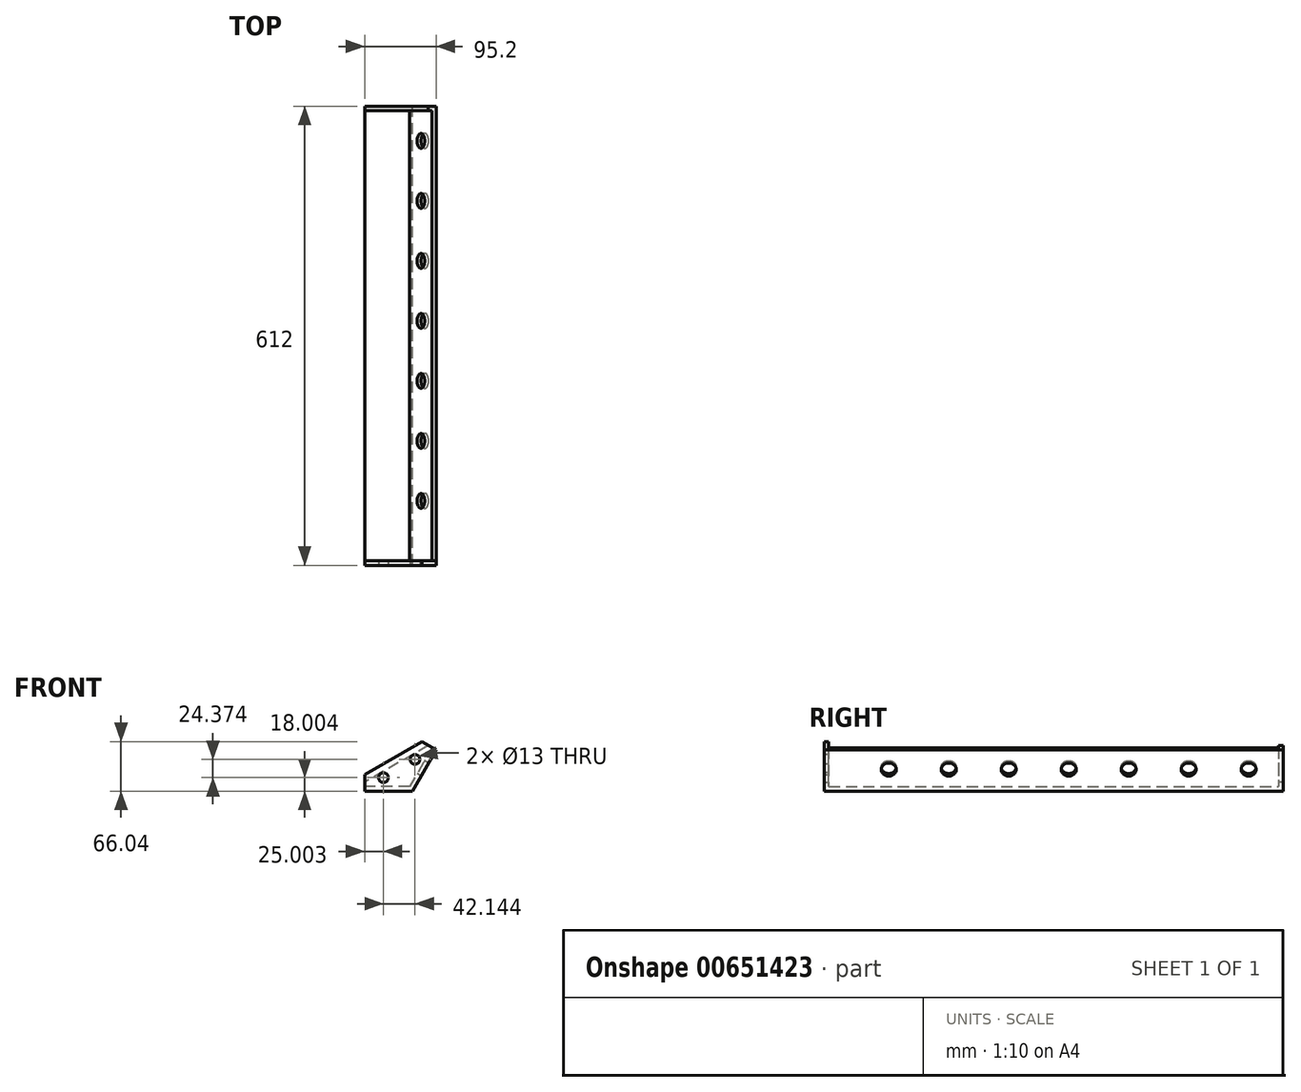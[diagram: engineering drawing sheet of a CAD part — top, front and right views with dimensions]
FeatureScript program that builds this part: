
annotation { "Feature Type Name" : "Feature", "Feature Type Description" : "" }
export const myFeature = defineFeature(function(context is Context, id is Id, definition is map)
    precondition{}
    {
        {
            var Q0;
            Q0=qCreatedBy(makeId("Front.planeOp"),FACE);
            var sketch = newSketch(context, id + "F0", { "sketchPlane" : qUnion([Q0])});
            skLineSegment(sketch, "E0", {"start": v(3.16, -10.39) * mm, "end": v(66.63, -10.39) * mm});
            skLineSegment(sketch, "E1", {"start": v(66.63, -10.39) * mm, "end": v(98.36, 44.58) * mm});
            skLineSegment(sketch, "E2", {"start": v(98.36, 44.58) * mm, "end": v(93.16, 47.58) * mm});
            skLineSegment(sketch, "E3", {"start": v(93.16, 47.58) * mm, "end": v(63.16, -4.39) * mm});
            skLineSegment(sketch, "E4", {"start": v(63.16, -4.39) * mm, "end": v(3.16, -4.39) * mm});
            skLineSegment(sketch, "E5", {"start": v(3.16, -4.39) * mm, "end": v(3.16, -10.39) * mm});
            skSolve(sketch);
        }
        {
            var Q0;
            Q0 = qSketchRegion(id + "F0", true);
            extrude(context, id + "F1", {"entities" : qUnion([Q0]), "depth" : 600 * mm, "offsetDistance" : 25 * mm});
        }
        {
            var Q0;
            Q0=makeQuery(id+"F1.opExtrude","CAP_FACE",FACE,{"disambiguationData":[OSD([sQuery(id+"F0.wireOp",EDGE,"E0"),sQuery(id+"F0.wireOp",EDGE,"E1"),sQuery(id+"F0.wireOp",EDGE,"E2"),sQuery(id+"F0.wireOp",EDGE,"E3"),sQuery(id+"F0.wireOp",EDGE,"E4"),sQuery(id+"F0.wireOp",EDGE,"E5")])],"isStart":true});
            var sketch = newSketch(context, id + "F2", { "sketchPlane" : qUnion([Q0])});
            skLineSegment(sketch, "E6", {"start": v(-3.16, 1.61) * mm, "end": v(-3.16, -10.39) * mm});
            skLineSegment(sketch, "E7", {"start": v(-98.36, 44.58) * mm, "end": v(-87.97, 50.58) * mm});
            skLineSegment(sketch, "E8", {"start": v(-87.97, 50.58) * mm, "end": v(-3.16, 1.61) * mm});
            skLineSegment(sketch, "E9", {"start": v(-98.36, 44.58) * mm, "end": v(-66.63, -10.39) * mm});
            skLineSegment(sketch, "E10", {"start": v(-66.63, -10.39) * mm, "end": v(-3.16, -10.39) * mm});
            skSolve(sketch);
        }
        {
            var Q0;
            Q0 = qSketchRegion(id + "F2", true);
            extrude(context, id + "F3", {"entities" : qUnion([Q0]), "operationType" : NewBodyOperationType.ADD, "depth" : 6 * mm, "offsetDistance" : 25 * mm});
        }
        {
            var Q0;
            Q0=makeQuery(id+"F1.opExtrude","SWEPT_FACE",FACE,{"disambiguationData":[OSD([sQuery(id+"F0.wireOp",EDGE,"E3")])]});
            var sketch = newSketch(context, id + "F4", { "sketchPlane" : qUnion([Q0])});
            skCircle(sketch, "E11", {"center": v(40, 57.78) * mm, "radius": 10 * mm});
            skCircle(sketch, "E12", {"center": v(120, 57.78) * mm, "radius": 10 * mm});
            skCircle(sketch, "E13", {"center": v(200, 57.78) * mm, "radius": 10 * mm});
            skCircle(sketch, "E14", {"center": v(360, 57.78) * mm, "radius": 10 * mm});
            skCircle(sketch, "E15", {"center": v(280, 57.78) * mm, "radius": 10 * mm});
            skCircle(sketch, "E16", {"center": v(520, 57.78) * mm, "radius": 10 * mm});
            skCircle(sketch, "E17", {"center": v(440, 57.78) * mm, "radius": 10 * mm});
            skSolve(sketch);
        }
        {
            var Q0;
            Q0 = qSketchRegion(id + "F4", true);
            extrude(context, id + "F5", {"entities" : qUnion([Q0]), "operationType" : NewBodyOperationType.REMOVE, "oppositeDirection" : true, "depth" : 25 * mm, "offsetDistance" : 25 * mm});
        }
        {
            var Q0;
            Q0=makeQuery(id+"F1.opExtrude","CAP_FACE",FACE,{"disambiguationData":[OSD([sQuery(id+"F0.wireOp",EDGE,"E0"),sQuery(id+"F0.wireOp",EDGE,"E1"),sQuery(id+"F0.wireOp",EDGE,"E2"),sQuery(id+"F0.wireOp",EDGE,"E3"),sQuery(id+"F0.wireOp",EDGE,"E4"),sQuery(id+"F0.wireOp",EDGE,"E5")])],"isStart":false});
            var sketch = newSketch(context, id + "F6", { "sketchPlane" : qUnion([Q0])});
            skLineSegment(sketch, "E18", {"start": v(3.16, -10.39) * mm, "end": v(3.16, 11.61) * mm});
            skLineSegment(sketch, "E19", {"start": v(3.16, 11.61) * mm, "end": v(79.35, 55.65) * mm});
            skLineSegment(sketch, "E20", {"start": v(79.35, 55.65) * mm, "end": v(98.36, 44.58) * mm});
            skLineSegment(sketch, "E21", {"start": v(98.36, 44.58) * mm, "end": v(66.63, -10.39) * mm});
            skLineSegment(sketch, "E22", {"start": v(66.63, -10.39) * mm, "end": v(3.16, -10.39) * mm});
            skSolve(sketch);
        }
        {
            var Q0;
            Q0 = qSketchRegion(id + "F6", true);
            extrude(context, id + "F7", {"entities" : qUnion([Q0]), "operationType" : NewBodyOperationType.ADD, "depth" : 6 * mm, "offsetDistance" : 25 * mm});
        }
        {
            var Q0;
            Q0=makeQuery(id+"F7.opExtrude","CAP_FACE",FACE,{"disambiguationData":[OSD([sQuery(id+"F6.wireOp",EDGE,"E18"),sQuery(id+"F6.wireOp",EDGE,"E19"),sQuery(id+"F6.wireOp",EDGE,"E20"),sQuery(id+"F6.wireOp",EDGE,"E21"),sQuery(id+"F6.wireOp",EDGE,"E22")])],"isStart":false});
            var sketch = newSketch(context, id + "F8", { "sketchPlane" : qUnion([Q0])});
            skCircle(sketch, "E23", {"center": v(70.3, 31.99) * mm, "radius": 6.5 * mm});
            skCircle(sketch, "E24", {"center": v(28.16, 7.61) * mm, "radius": 6.5 * mm});
            skSolve(sketch);
        }
        {
            var Q0;
            Q0 = qSketchRegion(id + "F8", true);
            extrude(context, id + "F9", {"entities" : qUnion([Q0]), "operationType" : NewBodyOperationType.REMOVE, "oppositeDirection" : true, "depth" : 25 * mm, "offsetDistance" : 25 * mm});
        }
    });
